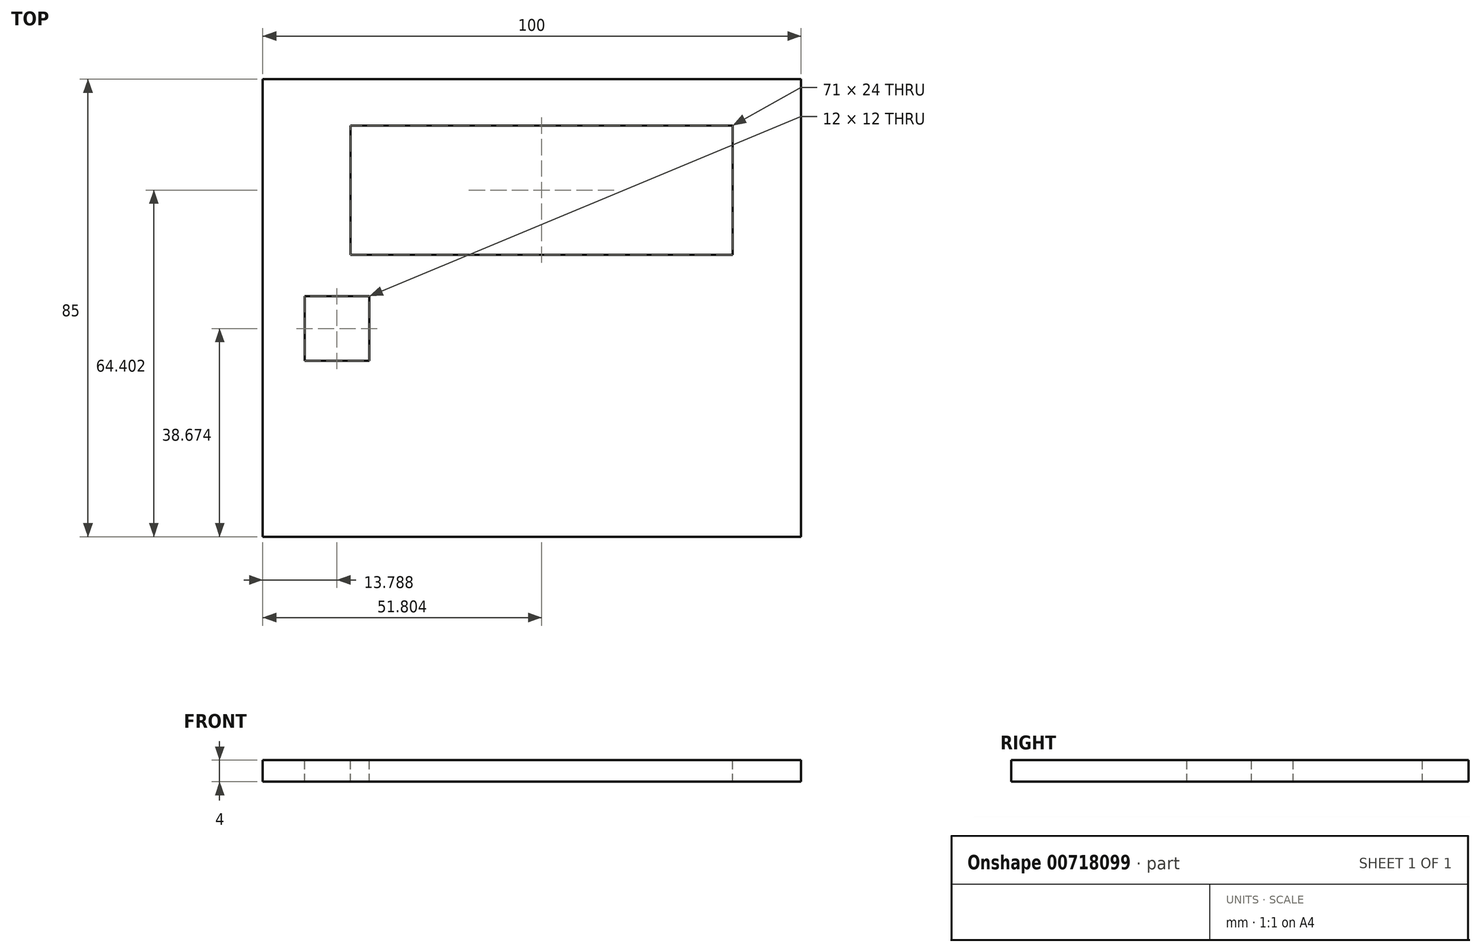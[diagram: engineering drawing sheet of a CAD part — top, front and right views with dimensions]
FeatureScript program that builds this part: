
annotation { "Feature Type Name" : "Feature", "Feature Type Description" : "" }
export const myFeature = defineFeature(function(context is Context, id is Id, definition is map)
    precondition{}
    {
        {
            var Q0;
            Q0=qCreatedBy(makeId("Top.planeOp"),FACE);
            var sketch = newSketch(context, id + "F0", { "sketchPlane" : qUnion([Q0])});
            skLineSegment(sketch, "E0.bottom", {"start": v(-49.31, 43.9) * mm, "end": v(50.69, 43.9) * mm});
            skLineSegment(sketch, "E0.top", {"start": v(-49.31, -41.1) * mm, "end": v(50.69, -41.1) * mm});
            skLineSegment(sketch, "E0.left", {"start": v(-49.31, 43.9) * mm, "end": v(-49.31, -41.1) * mm});
            skLineSegment(sketch, "E0.right", {"start": v(50.69, 43.9) * mm, "end": v(50.69, -41.1) * mm});
            skPoint(sketch, "E0.middle", {"position": v(0.69, 1.4) * mm});
            skSolve(sketch);
        }
        {
            var Q0;
            Q0 = qSketchRegion(id + "F0", true);
            extrude(context, id + "F1", {"entities" : qUnion([Q0]), "depth" : 4 * mm, "offsetDistance" : 25 * mm});
        }
        {
            var Q0;
            Q0=makeQuery(id+"F1.opExtrude","CAP_FACE",FACE,{"disambiguationData":[OSD([sQuery(id+"F0.wireOp",EDGE,"E0.bottom"),sQuery(id+"F0.wireOp",EDGE,"E0.top"),sQuery(id+"F0.wireOp",EDGE,"E0.left"),sQuery(id+"F0.wireOp",EDGE,"E0.right")])],"isStart":false});
            var sketch = newSketch(context, id + "F2", { "sketchPlane" : qUnion([Q0])});
            skLineSegment(sketch, "E1.bottom", {"start": v(-33, 35.31) * mm, "end": v(38, 35.31) * mm});
            skLineSegment(sketch, "E1.top", {"start": v(-33, 11.31) * mm, "end": v(38, 11.31) * mm});
            skLineSegment(sketch, "E1.left", {"start": v(-33, 35.31) * mm, "end": v(-33, 11.31) * mm});
            skLineSegment(sketch, "E1.right", {"start": v(38, 35.31) * mm, "end": v(38, 11.31) * mm});
            skPoint(sketch, "E1.middle", {"position": v(2.5, 23.31) * mm});
            skSolve(sketch);
        }
        {
            var Q0;
            Q0 = qSketchRegion(id + "F2", true);
            extrude(context, id + "F3", {"entities" : qUnion([Q0]), "operationType" : NewBodyOperationType.REMOVE, "oppositeDirection" : true, "depth" : 4 * mm, "offsetDistance" : 25 * mm});
        }
        {
            var Q0;
            Q0=makeQuery(id+"F1.opExtrude","CAP_FACE",FACE,{"disambiguationData":[OSD([sQuery(id+"F0.wireOp",EDGE,"E0.bottom"),sQuery(id+"F0.wireOp",EDGE,"E0.top"),sQuery(id+"F0.wireOp",EDGE,"E0.left"),sQuery(id+"F0.wireOp",EDGE,"E0.right")])],"isStart":false});
            var sketch = newSketch(context, id + "F4", { "sketchPlane" : qUnion([Q0])});
            skLineSegment(sketch, "E2.bottom", {"start": v(-29.52, -8.42) * mm, "end": v(-41.52, -8.42) * mm});
            skLineSegment(sketch, "E2.top", {"start": v(-29.52, 3.58) * mm, "end": v(-41.52, 3.58) * mm});
            skLineSegment(sketch, "E2.left", {"start": v(-29.52, -8.42) * mm, "end": v(-29.52, 3.58) * mm});
            skLineSegment(sketch, "E2.right", {"start": v(-41.52, -8.42) * mm, "end": v(-41.52, 3.58) * mm});
            skPoint(sketch, "E2.middle", {"position": v(-35.52, -2.42) * mm});
            skSolve(sketch);
        }
        {
            var Q0;
            Q0 = qSketchRegion(id + "F4", true);
            extrude(context, id + "F5", {"entities" : qUnion([Q0]), "operationType" : NewBodyOperationType.REMOVE, "oppositeDirection" : true, "depth" : 4 * mm, "offsetDistance" : 25 * mm});
        }
    });
